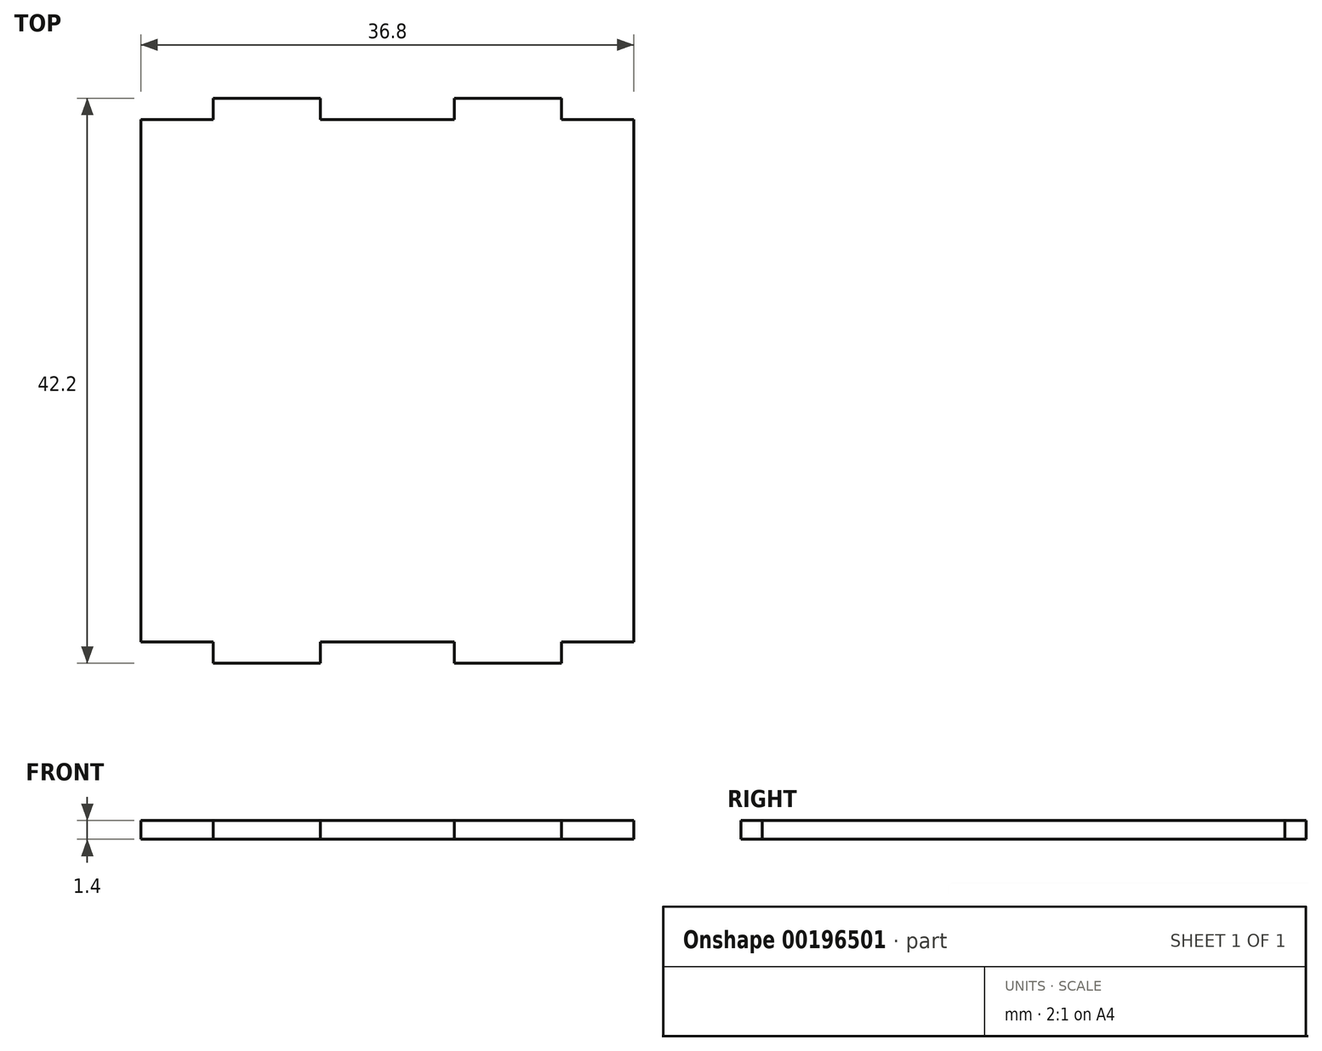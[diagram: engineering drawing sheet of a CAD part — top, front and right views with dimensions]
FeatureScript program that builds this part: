
annotation { "Feature Type Name" : "Feature", "Feature Type Description" : "" }
export const myFeature = defineFeature(function(context is Context, id is Id, definition is map)
    precondition{}
    {
        {
            var Q0;
            Q0=qCreatedBy(makeId("Top.planeOp"),FACE);
            var sketch = newSketch(context, id + "F0", { "sketchPlane" : qUnion([Q0])});
            skLineSegment(sketch, "E0.bottom", {"start": v(-18.4, 19.5) * mm, "end": v(18.4, 19.5) * mm});
            skLineSegment(sketch, "E0.top", {"start": v(-18.4, -19.5) * mm, "end": v(18.4, -19.5) * mm});
            skLineSegment(sketch, "E0.left", {"start": v(-18.4, 19.5) * mm, "end": v(-18.4, -19.5) * mm});
            skLineSegment(sketch, "E0.right", {"start": v(18.4, 19.5) * mm, "end": v(18.4, -19.5) * mm});
            skPoint(sketch, "E0.middle", {"position": v(0, 0) * mm});
            skLineSegment(sketch, "E1.bottom", {"start": v(-13, 19.5) * mm, "end": v(-5, 19.5) * mm});
            skLineSegment(sketch, "E1.top", {"start": v(-13, 21.1) * mm, "end": v(-5, 21.1) * mm});
            skLineSegment(sketch, "E1.left", {"start": v(-13, 19.5) * mm, "end": v(-13, 21.1) * mm});
            skLineSegment(sketch, "E1.right", {"start": v(-5, 19.5) * mm, "end": v(-5, 21.1) * mm});
            skLineSegment(sketch, "E2.MirrorCS", {"start": v(-13, -21.1) * mm, "end": v(-5, -21.1) * mm});
            skLineSegment(sketch, "E3.MirrorCS", {"start": v(-5, -19.5) * mm, "end": v(-5, -21.1) * mm});
            skLineSegment(sketch, "E4.MirrorCS", {"start": v(-13, -19.5) * mm, "end": v(-13, -21.1) * mm});
            skLineSegment(sketch, "E5.MirrorCS", {"start": v(5, 19.5) * mm, "end": v(5, 21.1) * mm});
            skLineSegment(sketch, "E6.MirrorCS", {"start": v(13, 21.1) * mm, "end": v(5, 21.1) * mm});
            skLineSegment(sketch, "E7.MirrorCS", {"start": v(13, 19.5) * mm, "end": v(13, 21.1) * mm});
            skLineSegment(sketch, "E8.MirrorCS", {"start": v(5, -19.5) * mm, "end": v(5, -21.1) * mm});
            skLineSegment(sketch, "E9.MirrorCS", {"start": v(13, -19.5) * mm, "end": v(13, -21.1) * mm});
            skLineSegment(sketch, "E10.MirrorCS", {"start": v(13, -21.1) * mm, "end": v(5, -21.1) * mm});
            skLineSegment(sketch, "E11", {"start": v(-28.95, 0) * mm, "end": v(37.18, 0) * mm, "construction": true});
            skPoint(sketch, "E11.endSnap0", {"position": v(-18.4, 0) * mm});
            skSolve(sketch);
        }
        {
            var Q0;
            Q0=sQuery(id+"F0.wireOp",EDGE,"E11");
            cPlane(context, id + "F1", {"entities" : qUnion([Q0]), "cplaneType" : CPlaneType.LINE_ANGLE, "offset" : 25 * mm, "angle" : 70 * degree, "width" : 150 * mm, "height" : 150 * mm});
        }
        {
            var Q0;
            {var subQ0=sQuery(id+"F0.wireOp",EDGE,"E8.MirrorCS");var subQ6=sQuery(id+"F0.wireOp",EDGE,"E5.MirrorCS");var subQ13=sQuery(id+"F0.wireOp",EDGE,"E0.left");Q0=qUnion([makeQuery(id+"F0.imprint","IMPRINT",FACE,{"disambiguationData":[TD([[makeQuery(id+"F0.imprint","IMPRINT",EDGE,{"derivedFrom":sQuery(id+"F0.wireOp",EDGE,"E2.MirrorCS")}),1.0]])]}),makeQuery(id+"F0.imprint","IMPRINT",FACE,{"disambiguationData":[TD([[makeQuery(id+"F0.imprint","IMPRINT",EDGE,{"derivedFrom":sQuery(id+"F0.wireOp",EDGE,"E1.top")}),-1.0]])]}),makeQuery(id+"F0.imprint","IMPRINT",FACE,{"disambiguationData":[TD([[makeQuery(id+"F0.imprint","IMPRINT",EDGE,{"derivedFrom":subQ13}),1.0]])]}),makeQuery(id+"F0.imprint","IMPRINT",FACE,{"disambiguationData":[TD([[makeQuery(id+"F0.imprint","IMPRINT",EDGE,{"derivedFrom":subQ6}),-1.0]])]}),makeQuery(id+"F0.imprint","IMPRINT",FACE,{"disambiguationData":[TD([[makeQuery(id+"F0.imprint","IMPRINT",EDGE,{"derivedFrom":subQ0}),1.0]])]})]);}
            extrude(context, id + "F2", {"entities" : qUnion([Q0]), "depth" : 1.4 * mm});
        }
    });
